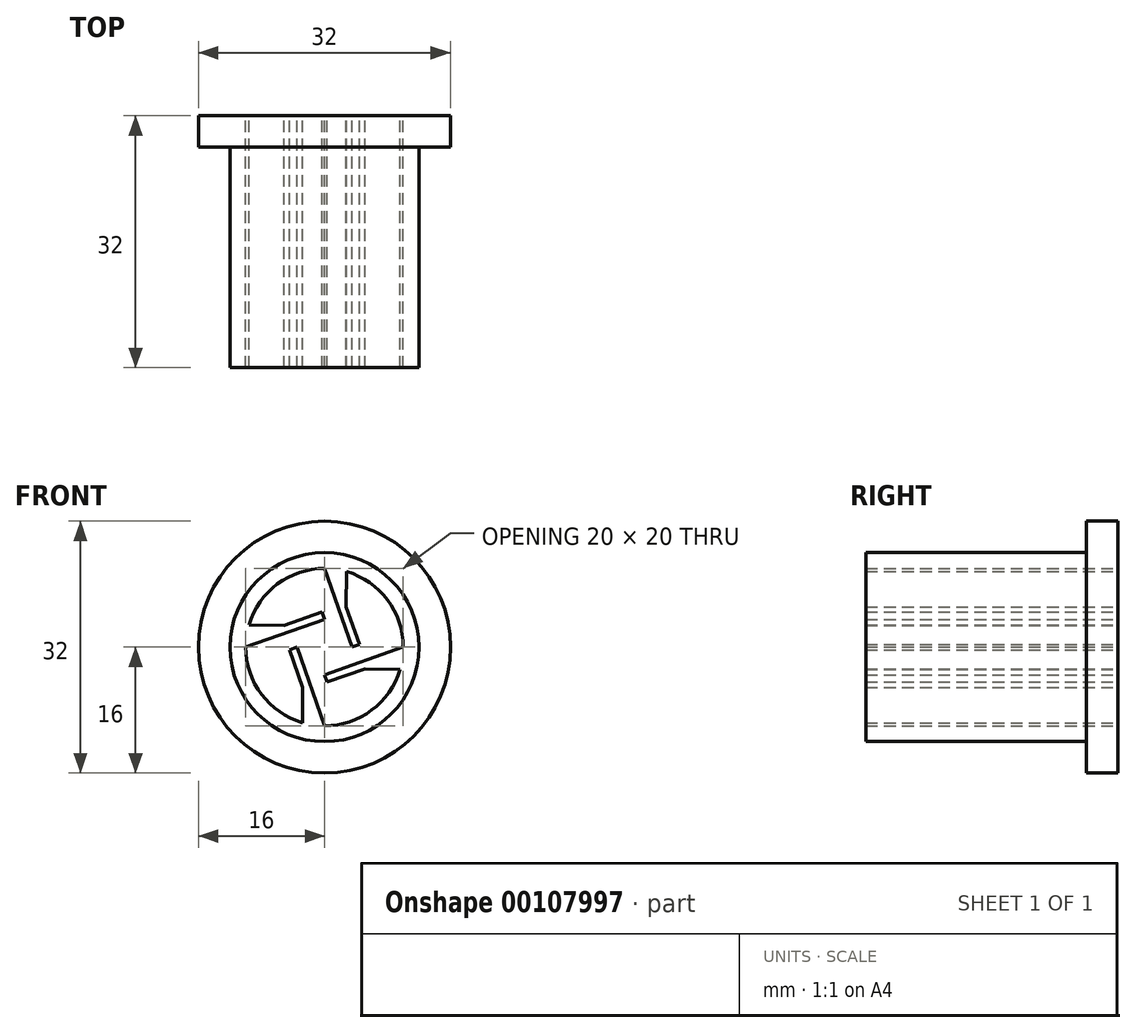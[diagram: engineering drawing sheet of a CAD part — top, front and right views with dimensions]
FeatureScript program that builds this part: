
annotation { "Feature Type Name" : "Feature", "Feature Type Description" : "" }
export const myFeature = defineFeature(function(context is Context, id is Id, definition is map)
    precondition{}
    {
        {
            var Q0;
            Q0=qCreatedBy(makeId("Front.planeOp"),FACE);
            var sketch = newSketch(context, id + "F0", { "sketchPlane" : qUnion([Q0])});
            skCircle(sketch, "E0", {"center": v(0, 0) * mm, "radius": 16 * mm});
            skCircle(sketch, "E1", {"center": v(0, 0) * mm, "radius": 12 * mm});
            skCircle(sketch, "E2", {"center": v(0, 0) * mm, "radius": 10 * mm});
            skLineSegment(sketch, "E3", {"start": v(0, 0) * mm, "end": v(0, 10) * mm, "construction": true});
            skLineSegment(sketch, "E4", {"start": v(0, 0) * mm, "end": v(-10, 0) * mm, "construction": true});
            skLineSegment(sketch, "E5", {"start": v(0, 0) * mm, "end": v(0, -10) * mm, "construction": true});
            skLineSegment(sketch, "E6", {"start": v(0, 0) * mm, "end": v(10, 0) * mm, "construction": true});
            skLineSegment(sketch, "E7", {"start": v(0, 3.5) * mm, "end": v(-10, 0) * mm});
            skLineSegment(sketch, "E8", {"start": v(0, 10) * mm, "end": v(3.5, 0) * mm});
            skLineSegment(sketch, "E9", {"start": v(10, 0) * mm, "end": v(0, -3.5) * mm});
            skLineSegment(sketch, "E10", {"start": v(0, -10) * mm, "end": v(-3.5, 0) * mm});
            skLineSegment(sketch, "E11", {"start": v(0, -3.5) * mm, "end": v(0.33, -4.44) * mm});
            skLineSegment(sketch, "E12", {"start": v(0.33, -4.44) * mm, "end": v(9.94, -1.08) * mm});
            skLineSegment(sketch, "E13", {"start": v(3.5, 0) * mm, "end": v(4.44, 0.33) * mm});
            skLineSegment(sketch, "E14", {"start": v(4.44, 0.33) * mm, "end": v(1.08, 9.94) * mm});
            skLineSegment(sketch, "E15", {"start": v(-3.5, 0) * mm, "end": v(-4.44, -0.33) * mm});
            skLineSegment(sketch, "E16", {"start": v(-4.44, -0.33) * mm, "end": v(-1.08, -9.94) * mm});
            skLineSegment(sketch, "E17", {"start": v(0, 3.5) * mm, "end": v(-0.33, 4.44) * mm});
            skLineSegment(sketch, "E18", {"start": v(-0.33, 4.44) * mm, "end": v(-9.94, 1.08) * mm});
            skLineSegment(sketch, "E19", {"start": v(-2.76, -5.14) * mm, "end": v(-2.82, -9.6) * mm});
            skLineSegment(sketch, "E20", {"start": v(-5.14, 2.76) * mm, "end": v(-9.6, 2.82) * mm});
            skLineSegment(sketch, "E21", {"start": v(2.76, 5.14) * mm, "end": v(2.82, 9.6) * mm});
            skLineSegment(sketch, "E22", {"start": v(5.14, -2.76) * mm, "end": v(9.6, -2.82) * mm});
            skCircle(sketch, "E23", {"center": v(0, 0) * mm, "radius": 3.25 * mm, "construction": true});
            skSolve(sketch);
        }
        {
            var Q0;
            Q0=qSketchRegion(id+"F0",true);
            var Q1;
            Q1=makeQuery(id+"F0.imprint","IMPRINT",FACE,{"disambiguationData":[TD([[makeQuery(id+"F0.imprint","IMPRINT",EDGE,{"derivedFrom":sQuery(id+"F0.wireOp",EDGE,"E1")}),1.0]])]});
            extrude(context, id + "F1", {"entities" : qUnion([Q0, Q1]), "depth" : 4 * mm});
        }
        {
            var Q0;
            Q0=makeQuery(id+"F0.imprint","IMPRINT",FACE,{"disambiguationData":[TD([[makeQuery(id+"F0.imprint","IMPRINT",EDGE,{"derivedFrom":sQuery(id+"F0.wireOp",EDGE,"E1")}),1.0]])]});
            var Q1;
            {var subQ0=sQuery(id+"F0.wireOp",EDGE,"E10");Q1=makeQuery(id+"F0.imprint","IMPRINT",FACE,{"disambiguationData":[TD([[makeQuery(id+"F0.imprint","IMPRINT",EDGE,{"derivedFrom":subQ0}),1.0]])]});}
            var Q2;
            {var subQ3=sQuery(id+"F0.wireOp",EDGE,"E19");Q2=makeQuery(id+"F0.imprint","IMPRINT",FACE,{"disambiguationData":[TD([[makeQuery(id+"F0.imprint","IMPRINT",EDGE,{"derivedFrom":subQ3}),1.0]])]});}
            var Q3;
            {var subQ3=sQuery(id+"F0.wireOp",EDGE,"E9");Q3=makeQuery(id+"F0.imprint","IMPRINT",FACE,{"disambiguationData":[TD([[makeQuery(id+"F0.imprint","IMPRINT",EDGE,{"derivedFrom":subQ3}),1.0]])]});}
            var Q4;
            {var subQ3=sQuery(id+"F0.wireOp",EDGE,"E22");Q4=makeQuery(id+"F0.imprint","IMPRINT",FACE,{"disambiguationData":[TD([[makeQuery(id+"F0.imprint","IMPRINT",EDGE,{"derivedFrom":subQ3}),1.0]])]});}
            var Q5;
            {var subQ0=sQuery(id+"F0.wireOp",EDGE,"E8");Q5=makeQuery(id+"F0.imprint","IMPRINT",FACE,{"disambiguationData":[TD([[makeQuery(id+"F0.imprint","IMPRINT",EDGE,{"derivedFrom":subQ0}),1.0]])]});}
            var Q6;
            {var subQ3=sQuery(id+"F0.wireOp",EDGE,"E21");Q6=makeQuery(id+"F0.imprint","IMPRINT",FACE,{"disambiguationData":[TD([[makeQuery(id+"F0.imprint","IMPRINT",EDGE,{"derivedFrom":subQ3}),1.0]])]});}
            var Q7;
            {var subQ3=sQuery(id+"F0.wireOp",EDGE,"E20");Q7=makeQuery(id+"F0.imprint","IMPRINT",FACE,{"disambiguationData":[TD([[makeQuery(id+"F0.imprint","IMPRINT",EDGE,{"derivedFrom":subQ3}),1.0]])]});}
            var Q8;
            {var subQ3=sQuery(id+"F0.wireOp",EDGE,"E7");Q8=makeQuery(id+"F0.imprint","IMPRINT",FACE,{"disambiguationData":[TD([[makeQuery(id+"F0.imprint","IMPRINT",EDGE,{"derivedFrom":subQ3}),-1.0]])]});}
            extrude(context, id + "F2", {"entities" : qUnion([Q0, Q1, Q2, Q3, Q4, Q5, Q6, Q7, Q8]), "operationType" : NewBodyOperationType.ADD, "depth" : 32 * mm});
        }
    });
